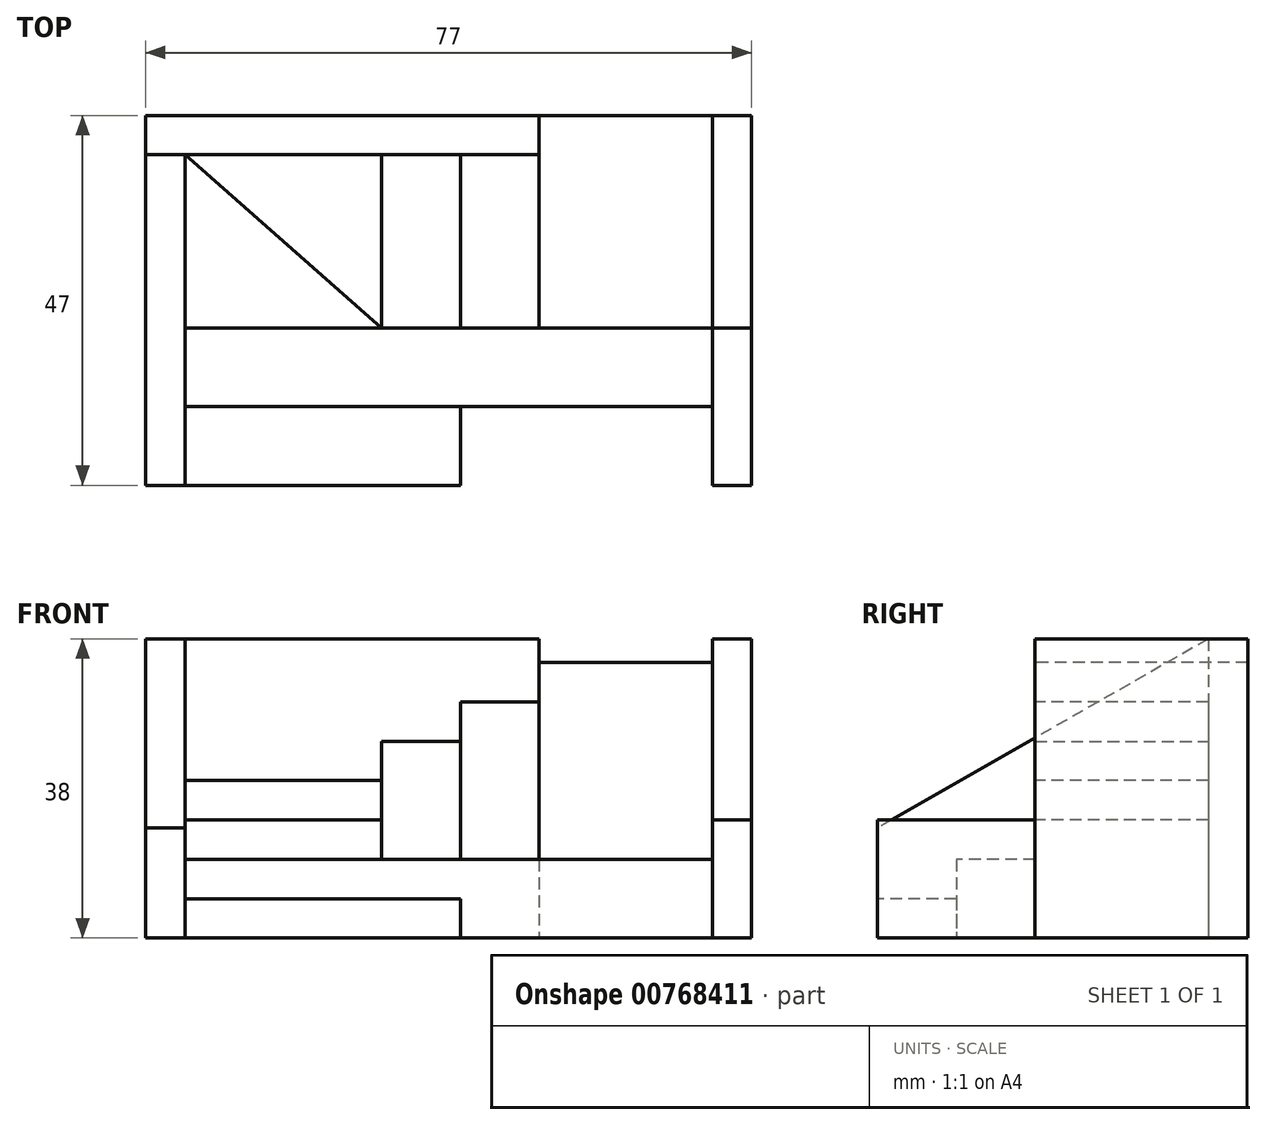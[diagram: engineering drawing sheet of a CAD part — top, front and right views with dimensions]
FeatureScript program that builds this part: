
annotation { "Feature Type Name" : "Feature", "Feature Type Description" : "" }
export const myFeature = defineFeature(function(context is Context, id is Id, definition is map)
    precondition{}
    {
        {
            var Q0;
            Q0=qCreatedBy(makeId("Top.planeOp"),FACE);
            var sketch = newSketch(context, id + "F0", { "sketchPlane" : qUnion([Q0])});
            skLineSegment(sketch, "E0.bottom", {"start": v(-38.5, 23.5) * mm, "end": v(38.5, 23.5) * mm});
            skLineSegment(sketch, "E0.top", {"start": v(-38.5, -23.5) * mm, "end": v(1.5, -23.5) * mm});
            skLineSegment(sketch, "E0.left", {"start": v(-38.5, 23.5) * mm, "end": v(-38.5, -23.5) * mm});
            skLineSegment(sketch, "E0.right", {"start": v(38.5, 23.5) * mm, "end": v(38.5, -23.5) * mm});
            skPoint(sketch, "E0.middle", {"position": v(0, 0) * mm});
            skLineSegment(sketch, "E1", {"start": v(-33.5, 18.5) * mm, "end": v(-33.5, -23.5) * mm});
            skLineSegment(sketch, "E2", {"start": v(-38.5, 18.5) * mm, "end": v(11.5, 18.5) * mm});
            skPoint(sketch, "E3.orphan", {"position": v(-33.5, 23.5) * mm});
            skLineSegment(sketch, "E4", {"start": v(-33.5, -13.5) * mm, "end": v(33.5, -13.5) * mm});
            skPoint(sketch, "E5.orphan", {"position": v(-38.5, -13.5) * mm});
            skLineSegment(sketch, "E6", {"start": v(33.5, 23.5) * mm, "end": v(33.5, -23.5) * mm});
            skLineSegment(sketch, "E7", {"start": v(-33.5, -3.5) * mm, "end": v(38.5, -3.5) * mm});
            skPoint(sketch, "E8.orphan", {"position": v(38.5, -13.5) * mm});
            skLineSegment(sketch, "E9", {"start": v(-33.5, 18.5) * mm, "end": v(-8.5, -3.5) * mm});
            skLineSegment(sketch, "E10", {"start": v(1.5, 18.5) * mm, "end": v(1.5, -3.5) * mm});
            skLineSegment(sketch, "E11", {"start": v(11.5, 18.5) * mm, "end": v(11.5, -3.5) * mm});
            skLineSegment(sketch, "E12.trimOffspring", {"start": v(33.5, -23.5) * mm, "end": v(38.5, -23.5) * mm});
            skLineSegment(sketch, "E13.trimOffspring", {"start": v(1.5, -13.5) * mm, "end": v(1.5, -23.5) * mm});
            skLineSegment(sketch, "E14.trimOffspring", {"start": v(-8.5, -3.5) * mm, "end": v(-8.5, 18.5) * mm});
            skLineSegment(sketch, "E15", {"start": v(11.5, 18.5) * mm, "end": v(11.5, 23.5) * mm});
            skSolve(sketch);
        }
        {
            var Q0;
            {var subQ0=sQuery(id+"F0.wireOp",EDGE,"E13.trimOffspring");Q0=makeQuery(id+"F0.imprint","IMPRINT",FACE,{"disambiguationData":[TD([[makeQuery(id+"F0.imprint","IMPRINT",EDGE,{"derivedFrom":subQ0}),-1.0]])]});}
            extrude(context, id + "F1", {"entities" : qUnion([Q0]), "depth" : 5 * mm, "offsetDistance" : 25 * mm});
        }
        {
            var Q0;
            {var subQ1=sQuery(id+"F0.wireOp",EDGE,"E4");var subQ6=sQuery(id+"F0.wireOp",EDGE,"E1");var subQ7=makeQuery(id+"F0.imprint","INTERSECT",VERTEX,{"derivedFrom":[subQ6,subQ1]});Q0=makeQuery(id+"F0.imprint","IMPRINT",FACE,{"disambiguationData":[TD([[makeQuery(id+"F0.imprint","IMPRINT",EDGE,{"disambiguationData":[TD([[subQ7,1.0]])],"derivedFrom":subQ6}),1.0]])]});}
            extrude(context, id + "F2", {"entities" : qUnion([Q0]), "depth" : 10 * mm, "offsetDistance" : 25 * mm});
        }
        {
            var Q0;
            {var subQ6=sQuery(id+"F0.wireOp",EDGE,"E12.trimOffspring");Q0=makeQuery(id+"F0.imprint","IMPRINT",FACE,{"disambiguationData":[TD([[makeQuery(id+"F0.imprint","IMPRINT",EDGE,{"derivedFrom":subQ6}),1.0]])]});}
            extrude(context, id + "F3", {"entities" : qUnion([Q0]), "operationType" : NewBodyOperationType.ADD, "depth" : 15 * mm, "offsetDistance" : 25 * mm});
        }
        {
            var Q0;
            {var subQ7=sQuery(id+"F0.wireOp",EDGE,"E15");Q0=makeQuery(id+"F0.imprint","IMPRINT",FACE,{"disambiguationData":[TD([[makeQuery(id+"F0.imprint","IMPRINT",EDGE,{"derivedFrom":subQ7}),1.0]])]});}
            extrude(context, id + "F4", {"entities" : qUnion([Q0]), "depth" : 38 * mm, "offsetDistance" : 25 * mm});
        }
        {
            var Q0;
            {var subQ5=sQuery(id+"F0.wireOp",EDGE,"E0.left");var subQ6=sQuery(id+"F0.wireOp",EDGE,"E0.top");var subQ7=makeQuery(id+"F0.imprint","INTERSECT",VERTEX,{"derivedFrom":[subQ6,subQ5]});Q0=makeQuery(id+"F0.imprint","IMPRINT",FACE,{"disambiguationData":[TD([[makeQuery(id+"F0.imprint","IMPRINT",EDGE,{"disambiguationData":[TD([[subQ7,-1.0]])],"derivedFrom":subQ6}),1.0]])]});}
            extrude(context, id + "F5", {"entities" : qUnion([Q0]), "depth" : 38 * mm, "offsetDistance" : 25 * mm});
        }
        {
            var Q0;
            Q0=makeQuery(id+"F5.opExtrude","SWEPT_FACE",FACE,{"disambiguationData":[OSD([sQuery(id+"F0.wireOp",EDGE,"E1")])]});
            var sketch = newSketch(context, id + "F6", { "sketchPlane" : qUnion([Q0])});
            skLineSegment(sketch, "E16", {"start": v(18.5, 38) * mm, "end": v(-23.5, 14) * mm});
            skSolve(sketch);
        }
        {
            var Q0;
            {var subQ0=sQuery(id+"F6.wireOp",EDGE,"E16");Q0=makeQuery(id+"F6.imprint","IMPRINT",FACE,{"disambiguationData":[TD([[makeQuery(id+"F6.imprint","IMPRINT",EDGE,{"derivedFrom":subQ0}),-1.0]])]});}
            extrude(context, id + "F7", {"entities" : qUnion([Q0]), "operationType" : NewBodyOperationType.REMOVE, "oppositeDirection" : true, "depth" : 5 * mm, "offsetDistance" : 25 * mm});
        }
        {
            var Q0;
            {var subQ0=sQuery(id+"F0.wireOp",EDGE,"E9");Q0=makeQuery(id+"F0.imprint","IMPRINT",FACE,{"disambiguationData":[TD([[makeQuery(id+"F0.imprint","IMPRINT",EDGE,{"derivedFrom":subQ0}),-1.0]])]});}
            extrude(context, id + "F8", {"entities" : qUnion([Q0]), "depth" : 15 * mm, "offsetDistance" : 25 * mm});
        }
        {
            var Q0;
            {var subQ0=sQuery(id+"F0.wireOp",EDGE,"E10");Q0=makeQuery(id+"F0.imprint","IMPRINT",FACE,{"disambiguationData":[TD([[makeQuery(id+"F0.imprint","IMPRINT",EDGE,{"derivedFrom":subQ0}),-1.0]])]});}
            extrude(context, id + "F9", {"entities" : qUnion([Q0]), "depth" : 25 * mm, "offsetDistance" : 25 * mm});
        }
        {
            var Q0;
            {var subQ2=sQuery(id+"F0.wireOp",EDGE,"E10");Q0=makeQuery(id+"F0.imprint","IMPRINT",FACE,{"disambiguationData":[TD([[makeQuery(id+"F0.imprint","IMPRINT",EDGE,{"derivedFrom":subQ2}),1.0]])]});}
            extrude(context, id + "F10", {"entities" : qUnion([Q0]), "depth" : 30 * mm, "offsetDistance" : 25 * mm});
        }
        {
            var Q0;
            {var subQ0=sQuery(id+"F0.wireOp",EDGE,"E11");Q0=makeQuery(id+"F0.imprint","IMPRINT",FACE,{"disambiguationData":[TD([[makeQuery(id+"F0.imprint","IMPRINT",EDGE,{"derivedFrom":subQ0}),1.0]])]});}
            extrude(context, id + "F11", {"entities" : qUnion([Q0]), "depth" : 35 * mm, "offsetDistance" : 25 * mm});
        }
        {
            var Q0;
            {var subQ0=sQuery(id+"F0.wireOp",EDGE,"E9");Q0=makeQuery(id+"F0.imprint","IMPRINT",FACE,{"disambiguationData":[TD([[makeQuery(id+"F0.imprint","IMPRINT",EDGE,{"derivedFrom":subQ0}),1.0]])]});}
            extrude(context, id + "F12", {"entities" : qUnion([Q0]), "depth" : 20 * mm, "offsetDistance" : 25 * mm});
        }
        {
            var Q0;
            {var subQ0=sQuery(id+"F0.wireOp",EDGE,"E0.right");var subQ1=sQuery(id+"F0.wireOp",EDGE,"E0.bottom");var subQ2=makeQuery(id+"F0.imprint","INTERSECT",VERTEX,{"derivedFrom":[subQ1,subQ0]});Q0=makeQuery(id+"F0.imprint","IMPRINT",FACE,{"disambiguationData":[TD([[makeQuery(id+"F0.imprint","IMPRINT",EDGE,{"disambiguationData":[TD([[subQ2,1.0]])],"derivedFrom":subQ1}),-1.0]])]});}
            extrude(context, id + "F13", {"entities" : qUnion([Q0]), "depth" : 38 * mm, "offsetDistance" : 25 * mm});
        }
    });
